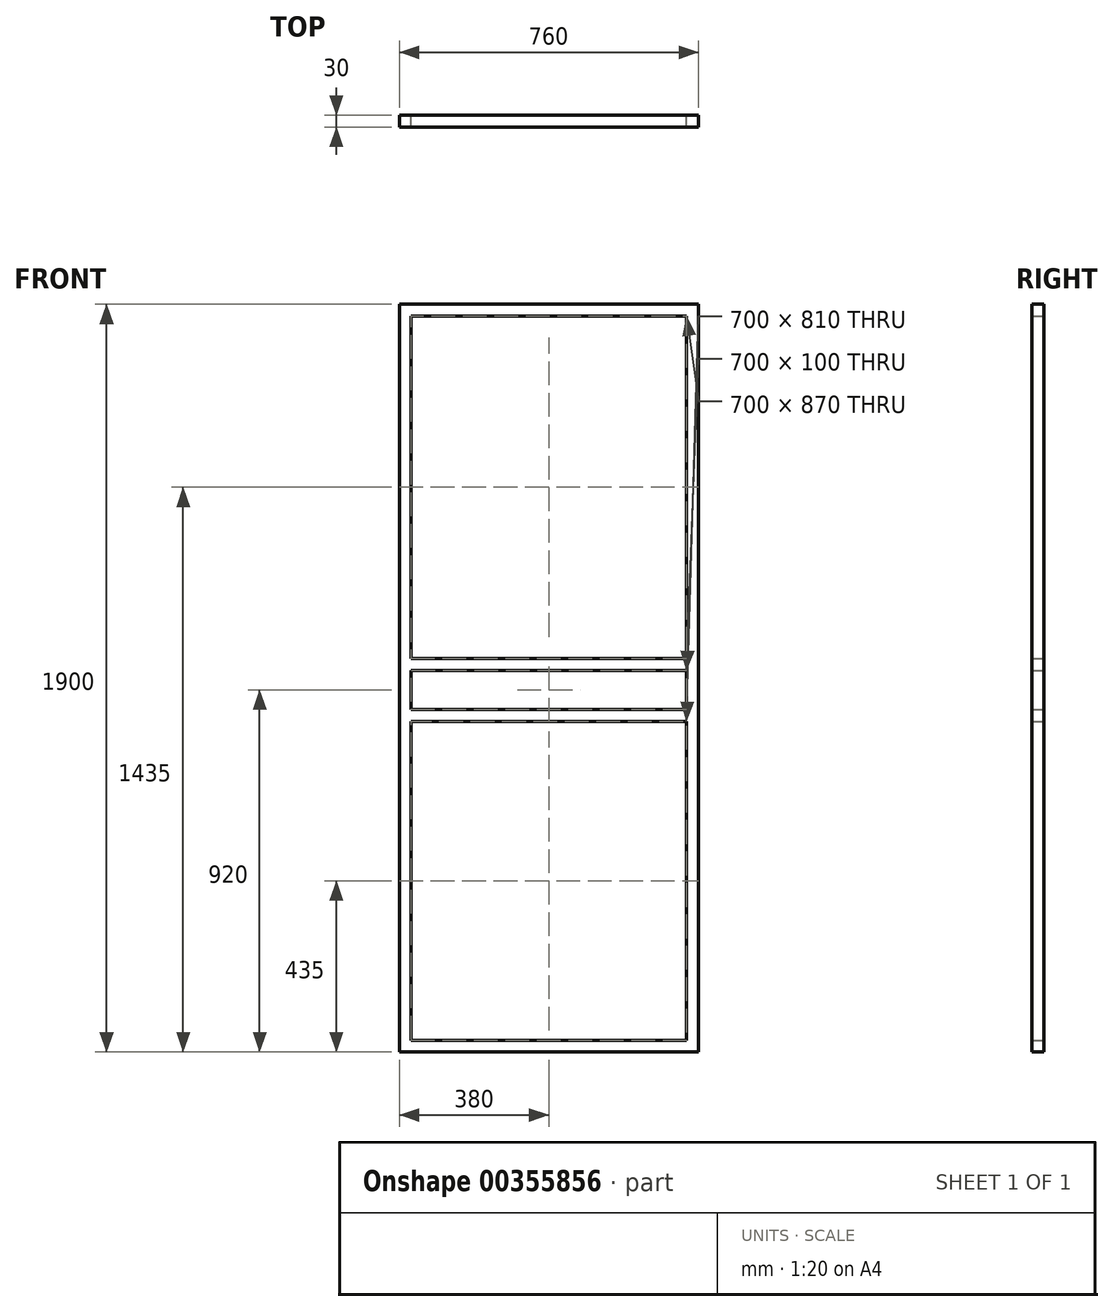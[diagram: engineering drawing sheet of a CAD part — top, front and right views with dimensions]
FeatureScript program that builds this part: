
annotation { "Feature Type Name" : "Feature", "Feature Type Description" : "" }
export const myFeature = defineFeature(function(context is Context, id is Id, definition is map)
    precondition{}
    {
        {
            var Q0;
            Q0=qCreatedBy(makeId("Front.planeOp"),FACE);
            var sketch = newSketch(context, id + "F0", { "sketchPlane" : qUnion([Q0])});
            skLineSegment(sketch, "E0.top", {"start": v(380, -900) * mm, "end": v(-380, -900) * mm});
            skLineSegment(sketch, "E0.left", {"start": v(380, 900) * mm, "end": v(380, -900) * mm});
            skLineSegment(sketch, "E0.right", {"start": v(-380, 900) * mm, "end": v(-380, -900) * mm});
            skPoint(sketch, "E0.middle", {"position": v(0, 0) * mm});
            skLineSegment(sketch, "E1.1", {"start": v(350, 870) * mm, "end": v(350, 100) * mm});
            skLineSegment(sketch, "E1.2", {"start": v(350, -870) * mm, "end": v(-350, -870) * mm});
            skLineSegment(sketch, "E1.3", {"start": v(-350, 870) * mm, "end": v(-350, 100) * mm});
            skLineSegment(sketch, "E2", {"start": v(0, -900) * mm, "end": v(0, 100) * mm, "construction": true});
            skPoint(sketch, "E2.endSnap0", {"position": v(0, -900) * mm});
            skLineSegment(sketch, "E3.bottom", {"start": v(-350, 100) * mm, "end": v(350, 100) * mm});
            skLineSegment(sketch, "E3.top", {"start": v(-350, 70) * mm, "end": v(350, 70) * mm});
            skLineSegment(sketch, "E4", {"start": v(-170.97, 70) * mm, "end": v(-170.97, -30) * mm, "construction": true});
            skLineSegment(sketch, "E5.bottom", {"start": v(-350, -30) * mm, "end": v(350, -30) * mm});
            skLineSegment(sketch, "E5.top", {"start": v(-350, -60) * mm, "end": v(350, -60) * mm});
            skLineSegment(sketch, "E6.trimOffspring", {"start": v(-350, 70) * mm, "end": v(-350, -30) * mm});
            skPoint(sketch, "E3.left.start.orphan", {"position": v(-368.05, 100) * mm});
            skLineSegment(sketch, "E7.trimOffspring", {"start": v(-350, -60) * mm, "end": v(-350, -870) * mm});
            skPoint(sketch, "E5.left.start.orphan", {"position": v(-366.7, -30) * mm});
            skLineSegment(sketch, "E8.trimOffspring", {"start": v(350, -60) * mm, "end": v(350, -870) * mm});
            skLineSegment(sketch, "E9.trimOffspring", {"start": v(350, 70) * mm, "end": v(350, -30) * mm});
            skLineSegment(sketch, "E10", {"start": v(380, 900) * mm, "end": v(380, 1000) * mm});
            skLineSegment(sketch, "E11", {"start": v(380, 1000) * mm, "end": v(-380, 1000) * mm});
            skLineSegment(sketch, "E12", {"start": v(-380, 1000) * mm, "end": v(-380, 900) * mm});
            skLineSegment(sketch, "E13", {"start": v(350, 870) * mm, "end": v(350, 970) * mm});
            skLineSegment(sketch, "E14", {"start": v(-350, 870) * mm, "end": v(-350, 970) * mm});
            skPoint(sketch, "E15.endSnap0", {"position": v(0, 1000) * mm});
            skLineSegment(sketch, "E16", {"start": v(350, 970) * mm, "end": v(-350, 970) * mm});
            skPoint(sketch, "E15.end.orphan", {"position": v(0, 970) * mm});
            skPoint(sketch, "E15.start.orphan", {"position": v(0, 1000) * mm});
            skSolve(sketch);
        }
        {
            var Q0;
            Q0 = qSketchRegion(id + "F0", true);
            extrude(context, id + "F1", {"entities" : qUnion([Q0]), "depth" : 30 * mm});
        }
    });
